FCSTD DOCUMENT  (FreeCAD 0.16R6706 (Git))
Label: LED_Leiste_Outline
License: All rights reserved
LicenseURL: http://de.wikipedia.org/wiki/Alle_Rechte_vorbehalten
objects: Sketcher::SketchObject×1
note: 1 computed .brp shape members not serialized (recipe doc carries the construction recipe); baked Part::Feature solids carry a one-line shape summary decoded from their .brp

FEATURE [Sketcher::SketchObject] Sketch
  sketch-geometry (8):
    g0: LineSegment StartX=-5.5 StartY=162 StartZ=0 EndX=5.5 EndY=162 EndZ=0
    g1: LineSegment StartX=5.5 StartY=162 StartZ=0 EndX=5.5 EndY=21 EndZ=0
    g2: LineSegment StartX=5.5 StartY=21 StartZ=0 EndX=13 EndY=21 EndZ=0
    g3: LineSegment StartX=13 StartY=21 StartZ=0 EndX=13 EndY=0 EndZ=0
    g4: LineSegment StartX=13 StartY=0 StartZ=0 EndX=-13 EndY=0 EndZ=0
    g5: LineSegment StartX=-13 StartY=0 StartZ=0 EndX=-13 EndY=21 EndZ=0
    g6: LineSegment StartX=-13 StartY=21 StartZ=0 EndX=-5.5 EndY=21 EndZ=0
    g7: LineSegment StartX=-5.5 StartY=21 StartZ=0 EndX=-5.5 EndY=162 EndZ=0
  constraints (23):
    c: Horizontal(g0)
    c: Coincident(g0,g1)
    c: Vertical(g1)
    c: Coincident(g1,g2)
    c: Horizontal(g2)
    c: Coincident(g2,g3)
    c: PointOnObject(g3,g-1)
    c: Vertical(g3)
    c: Coincident(g3,g4)
    c: PointOnObject(g4,g-1)
    c: Coincident(g4,g5)
    c: Vertical(g5)
    c: Coincident(g5,g6)
    c: Horizontal(g6)
    c: Coincident(g6,g7)
    c: Vertical(g7)
    c: Symmetric(g4,g3,g-2)
    c: Symmetric(g6,g1,g-2)
    c: Coincident(g7,g0)
    c: DistanceX(g0,g0) = 11
    c: DistanceX(g4,g3) = 26
    c: DistanceY(g3,g2) = 21
    c: DistanceY(g4,g0) = 162
